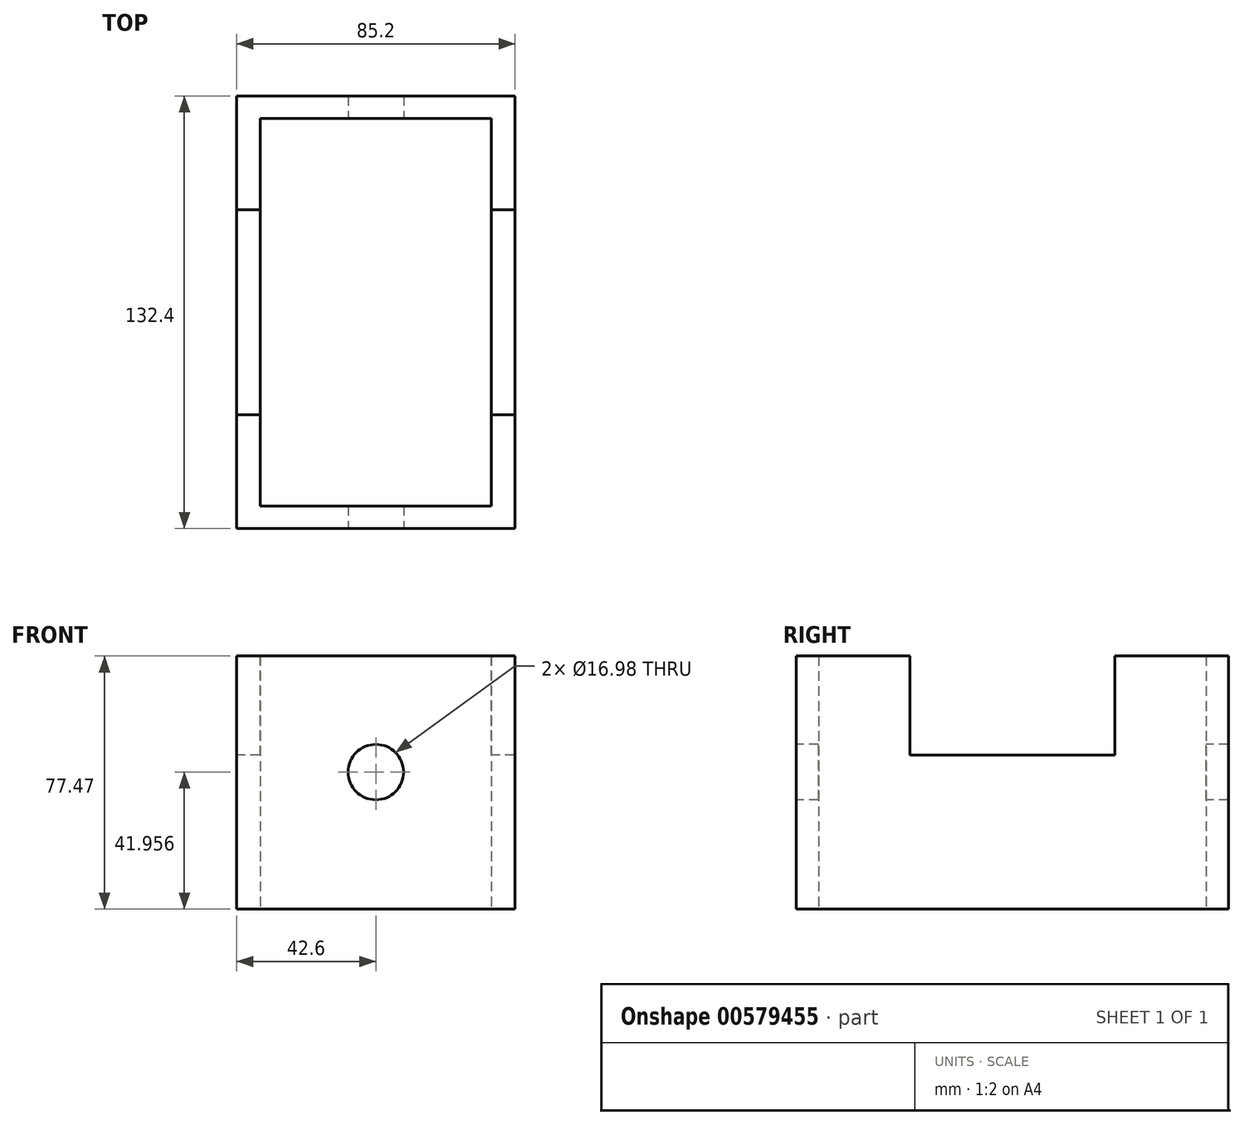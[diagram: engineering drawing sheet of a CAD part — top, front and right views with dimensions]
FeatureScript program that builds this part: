
annotation { "Feature Type Name" : "Feature", "Feature Type Description" : "" }
export const myFeature = defineFeature(function(context is Context, id is Id, definition is map)
    precondition{}
    {
        {
            var Q0;
            Q0=qCreatedBy(makeId("Top.planeOp"),FACE);
            var sketch = newSketch(context, id + "F0", { "sketchPlane" : qUnion([Q0])});
            skLineSegment(sketch, "E0.bottom", {"start": v(42.6, -66.2) * mm, "end": v(-42.6, -66.2) * mm});
            skLineSegment(sketch, "E0.top", {"start": v(42.6, 66.2) * mm, "end": v(-42.6, 66.2) * mm});
            skLineSegment(sketch, "E0.left", {"start": v(42.6, -66.2) * mm, "end": v(42.6, 66.2) * mm});
            skLineSegment(sketch, "E0.right", {"start": v(-42.6, -66.2) * mm, "end": v(-42.6, 66.2) * mm});
            skPoint(sketch, "E0.middle", {"position": v(0, 0) * mm});
            skLineSegment(sketch, "E1.bottom", {"start": v(35.4, -59.29) * mm, "end": v(-35.4, -59.29) * mm});
            skLineSegment(sketch, "E1.top", {"start": v(35.4, 59.29) * mm, "end": v(-35.4, 59.29) * mm});
            skLineSegment(sketch, "E1.left", {"start": v(35.4, -59.29) * mm, "end": v(35.4, 59.29) * mm});
            skLineSegment(sketch, "E1.right", {"start": v(-35.4, -59.29) * mm, "end": v(-35.4, 59.29) * mm});
            skSolve(sketch);
        }
        {
            var Q0;
            Q0=makeQuery(id+"F0.imprint","IMPRINT",FACE,{"disambiguationData":[TD([[makeQuery(id+"F0.imprint","IMPRINT",EDGE,{"derivedFrom":sQuery(id+"F0.wireOp",EDGE,"E0.bottom")}),-1.0]])]});
            extrude(context, id + "F1", {"entities" : qUnion([Q0]), "depth" : 88.4 * mm, "offsetDistance" : 25.4 * mm});
        }
        {
            var Q0;
            Q0=makeQuery(id+"F1.opExtrude","SWEPT_FACE",FACE,{"disambiguationData":[OSD([sQuery(id+"F0.wireOp",EDGE,"E0.right")])]});
            var sketch = newSketch(context, id + "F2", { "sketchPlane" : qUnion([Q0])});
            skLineSegment(sketch, "E2.bottom", {"start": v(31.4, 47.13) * mm, "end": v(-31.4, 47.13) * mm});
            skLineSegment(sketch, "E2.top", {"start": v(31.4, 88.16) * mm, "end": v(-31.4, 88.16) * mm});
            skLineSegment(sketch, "E2.left", {"start": v(31.4, 47.13) * mm, "end": v(31.4, 88.16) * mm});
            skLineSegment(sketch, "E2.right", {"start": v(-31.4, 47.13) * mm, "end": v(-31.4, 88.16) * mm});
            skPoint(sketch, "E2.middle", {"position": v(0, 67.64) * mm});
            skSolve(sketch);
        }
        {
            var Q0;
            Q0=makeQuery(id+"F2.imprint","IMPRINT",FACE,{"disambiguationData":[TD([[makeQuery(id+"F2.imprint","IMPRINT",EDGE,{"derivedFrom":sQuery(id+"F2.wireOp",EDGE,"E2.bottom")}),-1.0]])]});
            extrude(context, id + "F3", {"entities" : qUnion([Q0]), "operationType" : NewBodyOperationType.REMOVE, "endBound" : BoundingType.THROUGH_ALL, "oppositeDirection" : true, "depth" : 25.4 * mm, "offsetDistance" : 25.4 * mm});
        }
        {
            var Q0;
            Q0=makeQuery(id+"F1.opExtrude","CAP_FACE",FACE,{"disambiguationData":[OSD([sQuery(id+"F0.wireOp",EDGE,"E0.bottom"),sQuery(id+"F0.wireOp",EDGE,"E0.top"),sQuery(id+"F0.wireOp",EDGE,"E0.left"),sQuery(id+"F0.wireOp",EDGE,"E0.right"),sQuery(id+"F0.wireOp",EDGE,"E1.bottom"),sQuery(id+"F0.wireOp",EDGE,"E1.top"),sQuery(id+"F0.wireOp",EDGE,"E1.left"),sQuery(id+"F0.wireOp",EDGE,"E1.right")])],"isStart":false});
            extrude(context, id + "F4", {"entities" : qUnion([Q0]), "operationType" : NewBodyOperationType.REMOVE, "oppositeDirection" : true, "depth" : 10.92 * mm, "offsetDistance" : 25.4 * mm});
        }
        {
            var Q0;
            Q0=makeQuery(id+"F1.opExtrude","SWEPT_FACE",FACE,{"disambiguationData":[OSD([sQuery(id+"F0.wireOp",EDGE,"E0.bottom")])]});
            var sketch = newSketch(context, id + "F5", { "sketchPlane" : qUnion([Q0])});
            skCircle(sketch, "E3", {"center": v(0, 41.96) * mm, "radius": 8.49 * mm});
            skSolve(sketch);
        }
        {
            var Q0;
            Q0=makeQuery(id+"F5.imprint","IMPRINT",FACE,{"disambiguationData":[TD([[makeQuery(id+"F5.imprint","IMPRINT",EDGE,{"derivedFrom":sQuery(id+"F5.wireOp",EDGE,"E3")}),1.0]])]});
            extrude(context, id + "F6", {"entities" : qUnion([Q0]), "operationType" : NewBodyOperationType.REMOVE, "endBound" : BoundingType.THROUGH_ALL, "oppositeDirection" : true, "depth" : 25.4 * mm, "offsetDistance" : 25.4 * mm});
        }
    });
